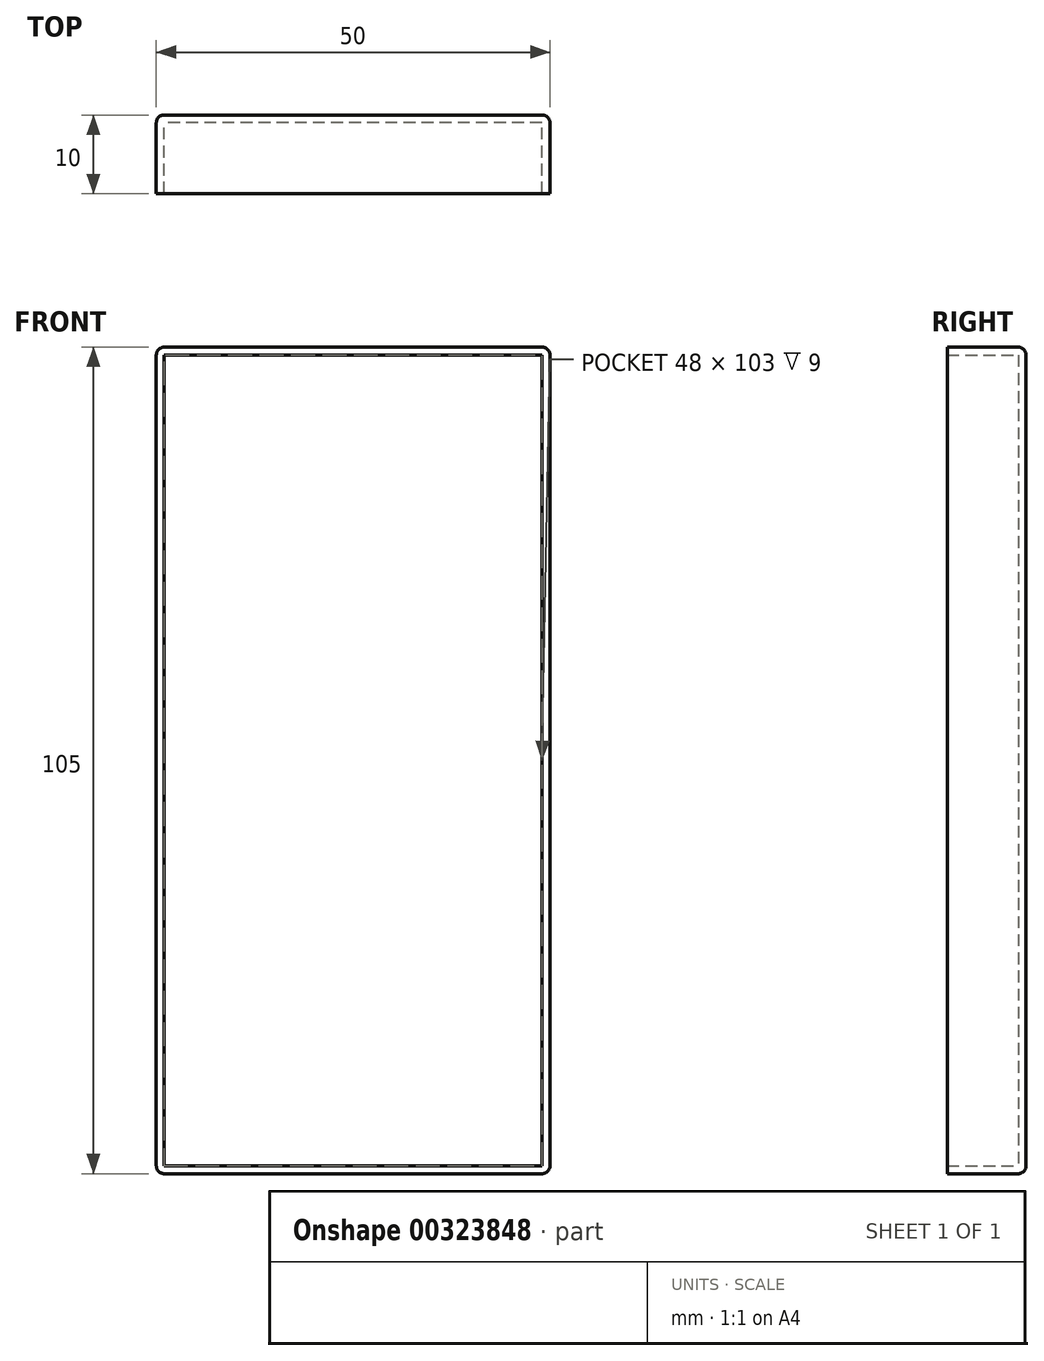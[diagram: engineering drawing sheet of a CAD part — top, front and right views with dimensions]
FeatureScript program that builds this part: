
annotation { "Feature Type Name" : "Feature", "Feature Type Description" : "" }
export const myFeature = defineFeature(function(context is Context, id is Id, definition is map)
    precondition{}
    {
        {
            var Q0;
            Q0=qCreatedBy(makeId("Front.planeOp"),FACE);
            var sketch = newSketch(context, id + "F0", { "sketchPlane" : qUnion([Q0])});
            skLineSegment(sketch, "E0.bottom", {"start": v(0, 105) * mm, "end": v(-50, 105) * mm});
            skLineSegment(sketch, "E0.top", {"start": v(0, 0) * mm, "end": v(-50, 0) * mm});
            skLineSegment(sketch, "E0.left", {"start": v(0, 105) * mm, "end": v(0, 0) * mm});
            skLineSegment(sketch, "E0.right", {"start": v(-50, 105) * mm, "end": v(-50, 0) * mm});
            skSolve(sketch);
        }
        {
            var Q0;
            Q0=makeQuery(id+"F0.imprint","IMPRINT",FACE,{"disambiguationData":[TD([[makeQuery(id+"F0.imprint","IMPRINT",EDGE,{"derivedFrom":sQuery(id+"F0.wireOp",EDGE,"E0.bottom")}),1.0]])]});
            extrude(context, id + "F1", {"entities" : qUnion([Q0]), "depth" : 10 * mm});
        }
        {
            var Q0;
            Q0=makeQuery(id+"F1.opExtrude","SWEPT_EDGE",EDGE,{"disambiguationData":[OSD([sQuery(id+"F0.wireOp",EDGE,"E0.bottom"),sQuery(id+"F0.wireOp",EDGE,"E0.right")])]});
            var Q1;
            Q1=makeQuery(id+"F1.opExtrude","SWEPT_EDGE",EDGE,{"disambiguationData":[OSD([sQuery(id+"F0.wireOp",EDGE,"E0.bottom"),sQuery(id+"F0.wireOp",EDGE,"E0.left")])]});
            var Q2;
            Q2=makeQuery(id+"F1.opExtrude","SWEPT_EDGE",EDGE,{"disambiguationData":[OSD([sQuery(id+"F0.wireOp",EDGE,"E0.top"),sQuery(id+"F0.wireOp",EDGE,"E0.left")])]});
            var Q3;
            Q3=makeQuery(id+"F1.opExtrude","SWEPT_EDGE",EDGE,{"disambiguationData":[OSD([sQuery(id+"F0.wireOp",EDGE,"E0.top"),sQuery(id+"F0.wireOp",EDGE,"E0.right")])]});
            fillet(context, id + "F2", {"entities" : qUnion([Q0, Q1, Q2, Q3]), "radius" : 1 * mm, "tangentPropagation" : true, "allowEdgeOverflow" : false});
        }
        {
            var Q0;
            Q0=makeQuery(id+"F1.opExtrude","CAP_EDGE",EDGE,{"disambiguationData":[OSD([sQuery(id+"F0.wireOp",EDGE,"E0.bottom")])],"isStart":true});
            fillet(context, id + "F3", {"entities" : qUnion([Q0]), "radius" : 1 * mm, "tangentPropagation" : true, "allowEdgeOverflow" : false});
        }
        {
            var Q0;
            Q0=makeQuery(id+"F1.opExtrude","CAP_FACE",FACE,{"disambiguationData":[OSD([sQuery(id+"F0.wireOp",EDGE,"E0.bottom"),sQuery(id+"F0.wireOp",EDGE,"E0.top"),sQuery(id+"F0.wireOp",EDGE,"E0.left"),sQuery(id+"F0.wireOp",EDGE,"E0.right")])],"isStart":false});
            shell(context, id + "F4", {"entities" : qUnion([Q0]), "thickness" : 1 * mm});
        }
    });
